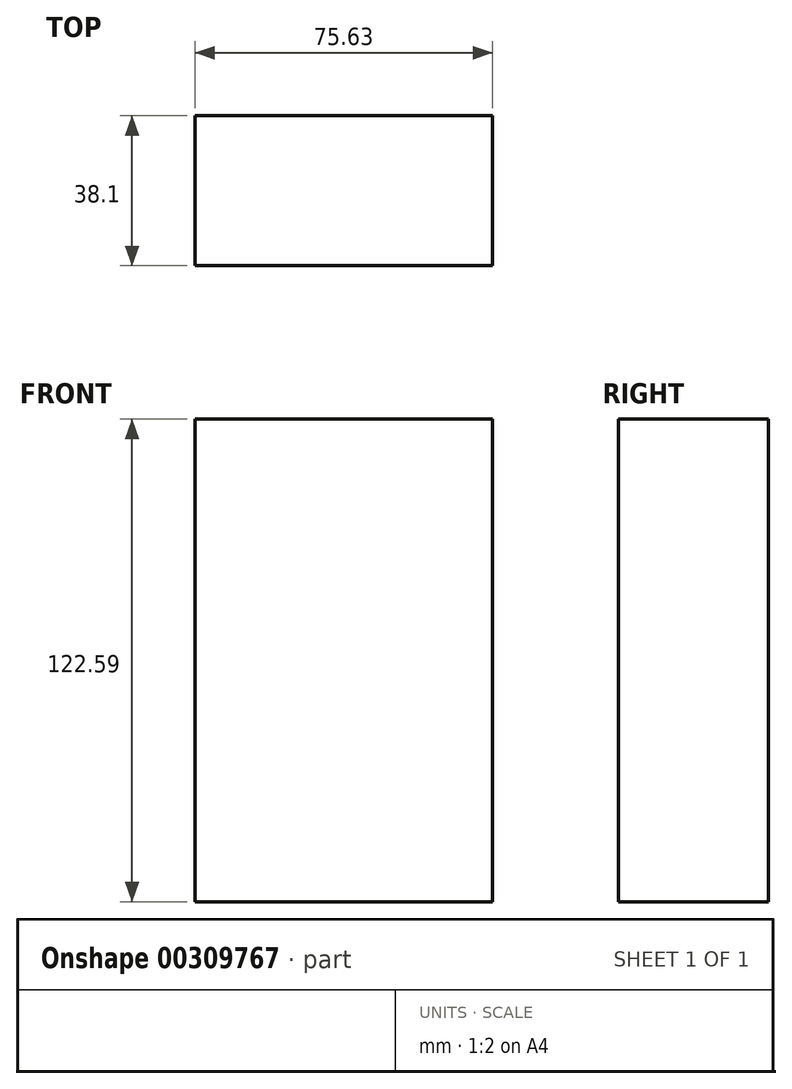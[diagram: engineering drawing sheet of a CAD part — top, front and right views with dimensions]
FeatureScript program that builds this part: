
annotation { "Feature Type Name" : "Feature", "Feature Type Description" : "" }
export const myFeature = defineFeature(function(context is Context, id is Id, definition is map)
    precondition{}
    {
        {
            var Q0;
            Q0=qCreatedBy(makeId("Front.planeOp"),FACE);
            var sketch = newSketch(context, id + "F0", { "sketchPlane" : qUnion([Q0])});
            skLineSegment(sketch, "E0.bottom", {"start": v(-66.83, 92.84) * mm, "end": v(8.8, 92.84) * mm});
            skLineSegment(sketch, "E0.top", {"start": v(-66.83, -29.75) * mm, "end": v(8.8, -29.75) * mm});
            skLineSegment(sketch, "E0.left", {"start": v(-66.83, 92.84) * mm, "end": v(-66.83, -29.75) * mm});
            skLineSegment(sketch, "E0.right", {"start": v(8.8, 92.84) * mm, "end": v(8.8, -29.75) * mm});
            skSolve(sketch);
        }
        {
            var Q0;
            Q0=makeQuery(id+"F0.imprint","IMPRINT",FACE,{"disambiguationData":[TD([[makeQuery(id+"F0.imprint","IMPRINT",EDGE,{"derivedFrom":sQuery(id+"F0.wireOp",EDGE,"E0.bottom")}),-1.0]])]});
            extrude(context, id + "F1", {"entities" : qUnion([Q0]), "depth" : 38.1 * mm, "offsetDistance" : 25.4 * mm});
        }
    });
